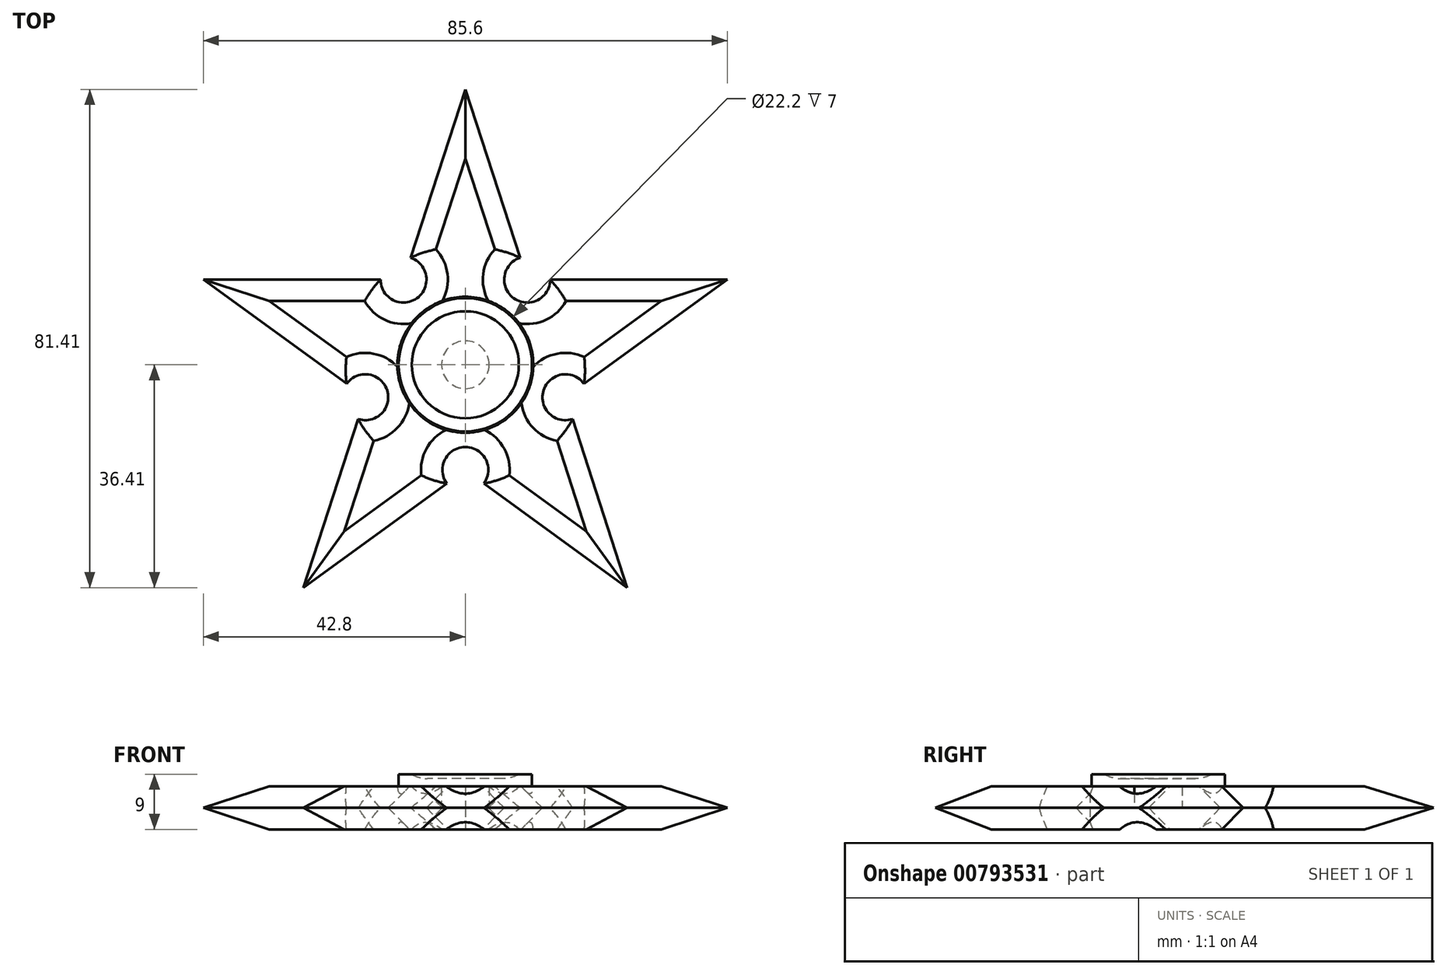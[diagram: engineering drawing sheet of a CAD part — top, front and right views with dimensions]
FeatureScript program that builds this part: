
annotation { "Feature Type Name" : "Feature", "Feature Type Description" : "" }
export const myFeature = defineFeature(function(context is Context, id is Id, definition is map)
    precondition{}
    {
        {
            assignVariable(context, id + "F0", {"name" : "BearingWidth", "anyValue" : 7});
        }
        {
            var Q0;
            Q0=qCreatedBy(makeId("Top.planeOp"),FACE);
            var sketch = newSketch(context, id + "F1", { "sketchPlane" : qUnion([Q0])});
            skCircle(sketch, "E0.cCircle", {"center": v(0, 0) * mm, "radius": 45 * mm, "construction": true});
            skLineSegment(sketch, "E0.0", {"start": v(0, 45) * mm, "end": v(42.8, 13.9) * mm, "construction": true});
            skLineSegment(sketch, "E0.1", {"start": v(42.8, 13.9) * mm, "end": v(26.45, -36.4) * mm, "construction": true});
            skLineSegment(sketch, "E0.2", {"start": v(26.45, -36.4) * mm, "end": v(-26.45, -36.4) * mm, "construction": true});
            skLineSegment(sketch, "E0.3", {"start": v(-26.45, -36.4) * mm, "end": v(-42.8, 13.9) * mm, "construction": true});
            skLineSegment(sketch, "E0.4", {"start": v(-42.8, 13.9) * mm, "end": v(0, 45) * mm, "construction": true});
            skCircle(sketch, "E1.cCircle", {"center": v(0, 0) * mm, "radius": 17.19 * mm, "construction": true});
            skLineSegment(sketch, "E1.0", {"start": v(0, -17.19) * mm, "end": v(-16.35, -5.31) * mm, "construction": true});
            skLineSegment(sketch, "E1.1", {"start": v(-16.35, -5.31) * mm, "end": v(-10.1, 13.9) * mm, "construction": true});
            skLineSegment(sketch, "E1.2", {"start": v(-10.1, 13.9) * mm, "end": v(10.1, 13.9) * mm, "construction": true});
            skLineSegment(sketch, "E1.3", {"start": v(10.1, 13.9) * mm, "end": v(16.35, -5.31) * mm, "construction": true});
            skLineSegment(sketch, "E1.4", {"start": v(16.35, -5.31) * mm, "end": v(0, -17.19) * mm, "construction": true});
            skLineSegment(sketch, "E2", {"start": v(0, 45) * mm, "end": v(-10.1, 13.9) * mm});
            skLineSegment(sketch, "E3", {"start": v(0, 45) * mm, "end": v(10.1, 13.9) * mm});
            skLineSegment(sketch, "E4", {"start": v(10.1, 13.9) * mm, "end": v(42.8, 13.9) * mm});
            skLineSegment(sketch, "E5", {"start": v(42.8, 13.9) * mm, "end": v(16.35, -5.31) * mm});
            skLineSegment(sketch, "E6", {"start": v(16.35, -5.31) * mm, "end": v(26.45, -36.4) * mm});
            skLineSegment(sketch, "E7", {"start": v(0, -17.19) * mm, "end": v(26.45, -36.4) * mm});
            skLineSegment(sketch, "E8", {"start": v(0, -17.19) * mm, "end": v(-26.45, -36.4) * mm});
            skLineSegment(sketch, "E9", {"start": v(-16.35, -5.31) * mm, "end": v(-26.45, -36.4) * mm});
            skLineSegment(sketch, "E10", {"start": v(-10.1, 13.9) * mm, "end": v(-42.8, 13.9) * mm});
            skLineSegment(sketch, "E11", {"start": v(-16.35, -5.31) * mm, "end": v(-42.8, 13.9) * mm});
            skCircle(sketch, "E12", {"center": v(0, 0) * mm, "radius": 11.1 * mm});
            skCircle(sketch, "E13", {"center": v(0, 0) * mm, "radius": 3.9 * mm});
            skCircle(sketch, "E14", {"center": v(-16.35, -5.31) * mm, "radius": 3.75 * mm});
            skCircle(sketch, "E15.1.0", {"center": v(0, -17.19) * mm, "radius": 3.75 * mm});
            skCircle(sketch, "E15.2.0", {"center": v(16.35, -5.31) * mm, "radius": 3.75 * mm});
            skCircle(sketch, "E15.3.0", {"center": v(10.1, 13.9) * mm, "radius": 3.75 * mm});
            skCircle(sketch, "E15.4.0", {"center": v(-10.1, 13.9) * mm, "radius": 3.75 * mm});
            skSolve(sketch);
        }
        {
            var Q0;
            Q0=makeQuery(id+"F1.imprint","IMPRINT",FACE,{"disambiguationData":[TD([[makeQuery(id+"F1.imprint","IMPRINT",EDGE,{"derivedFrom":sQuery(id+"F1.wireOp",EDGE,"E12")}),-1.0]])]});
            extrude(context, id + "F2", {"entities" : qUnion([Q0]), "endBound" : BoundingType.SYMMETRIC, "depth" : (getVariable(context, 'BearingWidth')) * mm, "offsetDistance" : 25 * mm});
        }
        {
            var Q0;
            Q0=makeQuery(id+"F1.imprint","IMPRINT",FACE,{"disambiguationData":[TD([[makeQuery(id+"F1.imprint","IMPRINT",EDGE,{"derivedFrom":sQuery(id+"F1.wireOp",EDGE,"E13")}),1.0]])]});
            extrude(context, id + "F3", {"entities" : qUnion([Q0]), "depth" : (getVariable(context, 'BearingWidth') / 2) * mm, "offsetDistance" : 25 * mm});
        }
        {
            var Q0;
            Q0=makeQuery(id+"F2.opExtrude","CAP_EDGE",EDGE,{"disambiguationData":[OSD([sQuery(id+"F1.wireOp",EDGE,"E8")])],"isStart":false});
            var Q1;
            Q1=makeQuery(id+"F2.opExtrude","CAP_EDGE",EDGE,{"disambiguationData":[OSD([sQuery(id+"F1.wireOp",EDGE,"E8")])],"isStart":true});
            var Q2;
            Q2=makeQuery(id+"F2.opExtrude","CAP_EDGE",EDGE,{"disambiguationData":[OSD([sQuery(id+"F1.wireOp",EDGE,"E9")])],"isStart":false});
            var Q3;
            Q3=makeQuery(id+"F2.opExtrude","CAP_EDGE",EDGE,{"disambiguationData":[OSD([sQuery(id+"F1.wireOp",EDGE,"E9")])],"isStart":true});
            var Q4;
            Q4=makeQuery(id+"F2.opExtrude","CAP_EDGE",EDGE,{"disambiguationData":[OSD([sQuery(id+"F1.wireOp",EDGE,"E11")])],"isStart":false});
            var Q5;
            Q5=makeQuery(id+"F2.opExtrude","CAP_EDGE",EDGE,{"disambiguationData":[OSD([sQuery(id+"F1.wireOp",EDGE,"E11")])],"isStart":true});
            var Q6;
            Q6=makeQuery(id+"F2.opExtrude","CAP_EDGE",EDGE,{"disambiguationData":[OSD([sQuery(id+"F1.wireOp",EDGE,"E10")])],"isStart":false});
            var Q7;
            Q7=makeQuery(id+"F2.opExtrude","CAP_EDGE",EDGE,{"disambiguationData":[OSD([sQuery(id+"F1.wireOp",EDGE,"E10")])],"isStart":true});
            var Q8;
            Q8=makeQuery(id+"F2.opExtrude","CAP_EDGE",EDGE,{"disambiguationData":[OSD([sQuery(id+"F1.wireOp",EDGE,"E2")])],"isStart":false});
            var Q9;
            Q9=makeQuery(id+"F2.opExtrude","CAP_EDGE",EDGE,{"disambiguationData":[OSD([sQuery(id+"F1.wireOp",EDGE,"E2")])],"isStart":true});
            var Q10;
            Q10=makeQuery(id+"F2.opExtrude","CAP_EDGE",EDGE,{"disambiguationData":[OSD([sQuery(id+"F1.wireOp",EDGE,"E3")])],"isStart":true});
            var Q11;
            Q11=makeQuery(id+"F2.opExtrude","CAP_EDGE",EDGE,{"disambiguationData":[OSD([sQuery(id+"F1.wireOp",EDGE,"E3")])],"isStart":false});
            var Q12;
            Q12=makeQuery(id+"F2.opExtrude","CAP_EDGE",EDGE,{"disambiguationData":[OSD([sQuery(id+"F1.wireOp",EDGE,"E4")])],"isStart":false});
            var Q13;
            Q13=makeQuery(id+"F2.opExtrude","CAP_EDGE",EDGE,{"disambiguationData":[OSD([sQuery(id+"F1.wireOp",EDGE,"E4")])],"isStart":true});
            var Q14;
            Q14=makeQuery(id+"F2.opExtrude","CAP_EDGE",EDGE,{"disambiguationData":[OSD([sQuery(id+"F1.wireOp",EDGE,"E5")])],"isStart":false});
            var Q15;
            Q15=makeQuery(id+"F2.opExtrude","CAP_EDGE",EDGE,{"disambiguationData":[OSD([sQuery(id+"F1.wireOp",EDGE,"E5")])],"isStart":true});
            var Q16;
            Q16=makeQuery(id+"F2.opExtrude","CAP_EDGE",EDGE,{"disambiguationData":[OSD([sQuery(id+"F1.wireOp",EDGE,"E6")])],"isStart":false});
            var Q17;
            Q17=makeQuery(id+"F2.opExtrude","CAP_EDGE",EDGE,{"disambiguationData":[OSD([sQuery(id+"F1.wireOp",EDGE,"E6")])],"isStart":true});
            var Q18;
            Q18=makeQuery(id+"F2.opExtrude","CAP_EDGE",EDGE,{"disambiguationData":[OSD([sQuery(id+"F1.wireOp",EDGE,"E7")])],"isStart":false});
            var Q19;
            Q19=makeQuery(id+"F2.opExtrude","CAP_EDGE",EDGE,{"disambiguationData":[OSD([sQuery(id+"F1.wireOp",EDGE,"E7")])],"isStart":true});
            var Q20;
            Q20=makeQuery(id+"F2.opExtrude","CAP_EDGE",EDGE,{"disambiguationData":[OSD([sQuery(id+"F1.wireOp",EDGE,"E15.4.0")])],"isStart":true});
            var Q21;
            Q21=makeQuery(id+"F2.opExtrude","CAP_EDGE",EDGE,{"disambiguationData":[OSD([sQuery(id+"F1.wireOp",EDGE,"E15.4.0")])],"isStart":false});
            var Q22;
            Q22=makeQuery(id+"F2.opExtrude","CAP_EDGE",EDGE,{"disambiguationData":[OSD([sQuery(id+"F1.wireOp",EDGE,"E15.3.0")])],"isStart":true});
            var Q23;
            Q23=makeQuery(id+"F2.opExtrude","CAP_EDGE",EDGE,{"disambiguationData":[OSD([sQuery(id+"F1.wireOp",EDGE,"E15.3.0")])],"isStart":false});
            var Q24;
            Q24=makeQuery(id+"F2.opExtrude","CAP_EDGE",EDGE,{"disambiguationData":[OSD([sQuery(id+"F1.wireOp",EDGE,"E15.2.0")])],"isStart":true});
            var Q25;
            Q25=makeQuery(id+"F2.opExtrude","CAP_EDGE",EDGE,{"disambiguationData":[OSD([sQuery(id+"F1.wireOp",EDGE,"E14")])],"isStart":true});
            var Q26;
            Q26=makeQuery(id+"F2.opExtrude","CAP_EDGE",EDGE,{"disambiguationData":[OSD([sQuery(id+"F1.wireOp",EDGE,"E15.1.0")])],"isStart":true});
            var Q27;
            Q27=makeQuery(id+"F2.opExtrude","CAP_EDGE",EDGE,{"disambiguationData":[OSD([sQuery(id+"F1.wireOp",EDGE,"E14")])],"isStart":false});
            var Q28;
            Q28=makeQuery(id+"F2.opExtrude","CAP_EDGE",EDGE,{"disambiguationData":[OSD([sQuery(id+"F1.wireOp",EDGE,"E15.1.0")])],"isStart":false});
            var Q29;
            Q29=makeQuery(id+"F2.opExtrude","CAP_EDGE",EDGE,{"disambiguationData":[OSD([sQuery(id+"F1.wireOp",EDGE,"E15.2.0")])],"isStart":false});
            chamfer(context, id + "F4", {"entities" : qUnion([Q0, Q1, Q2, Q3, Q4, Q5, Q6, Q7, Q8, Q9, Q10, Q11, Q12, Q13, Q14, Q15, Q16, Q17, Q18, Q19, Q20, Q21, Q22, Q23, Q24, Q25, Q26, Q27, Q28, Q29]), "width" : (getVariable(context, 'BearingWidth') / 2) * mm, "tangentPropagation" : true});
        }
        {
            var Q0;
            Q0=makeQuery(id+"F3.opExtrude","CAP_FACE",FACE,{"disambiguationData":[OSD([sQuery(id+"F1.wireOp",EDGE,"E13")])],"isStart":false});
            var sketch = newSketch(context, id + "F5", { "sketchPlane" : qUnion([Q0])});
            skCircle(sketch, "E16", {"center": v(0, 0) * mm, "radius": 10.9 * mm});
            skSolve(sketch);
        }
        {
            var Q0;
            Q0=makeQuery(id+"F5.imprint","IMPRINT",FACE,{"disambiguationData":[TD([[makeQuery(id+"F5.imprint","IMPRINT",EDGE,{"derivedFrom":sQuery(id+"F5.wireOp",EDGE,"E16")}),1.0]])]});
            var Q1;
            Q1=makeQuery(id+"F5.imprint","IMPRINT",FACE,{"disambiguationData":[TD([[makeQuery(id+"F5.imprint","IMPRINT",EDGE,{"derivedFrom":makeQuery(id+"F3.opExtrude","CAP_EDGE",EDGE,{"disambiguationData":[OSD([sQuery(id+"F1.wireOp",EDGE,"E13")])],"isStart":false})}),1.0]])]});
            extrude(context, id + "F6", {"entities" : qUnion([Q0, Q1]), "operationType" : NewBodyOperationType.ADD, "depth" : 2 * mm, "offsetDistance" : 25 * mm});
        }
        {
            var Q0;
            Q0=makeQuery(id+"F6.opExtrude","CAP_FACE",FACE,{"disambiguationData":[OSD([sQuery(id+"F5.wireOp",EDGE,"E16")])],"isStart":false});
            var sketch = newSketch(context, id + "F7", { "sketchPlane" : qUnion([Q0])});
            skCircle(sketch, "E17", {"center": v(0, 0) * mm, "radius": 8.74 * mm});
            skSolve(sketch);
        }
        {
            var Q0;
            Q0=makeQuery(id+"F7.imprint","IMPRINT",FACE,{"disambiguationData":[TD([[makeQuery(id+"F7.imprint","IMPRINT",EDGE,{"derivedFrom":sQuery(id+"F7.wireOp",EDGE,"E17")}),1.0]])]});
            extrude(context, id + "F8", {"entities" : qUnion([Q0]), "operationType" : NewBodyOperationType.REMOVE, "oppositeDirection" : true, "depth" : 0.7 * mm, "offsetDistance" : 25 * mm});
        }
        {
            var Q0;
            Q0=makeQuery(id+"F8.boolean.opBoolean","COPY",EDGE,{"derivedFrom":makeQuery(id+"F8.opExtrude","CAP_EDGE",EDGE,{"disambiguationData":[OSD([sQuery(id+"F7.wireOp",EDGE,"E17")])],"isStart":false})});
            fillet(context, id + "F9", {"entities" : qUnion([Q0]), "radius" : 5 * mm, "tangentPropagation" : true, "allowEdgeOverflow" : false});
        }
    });
